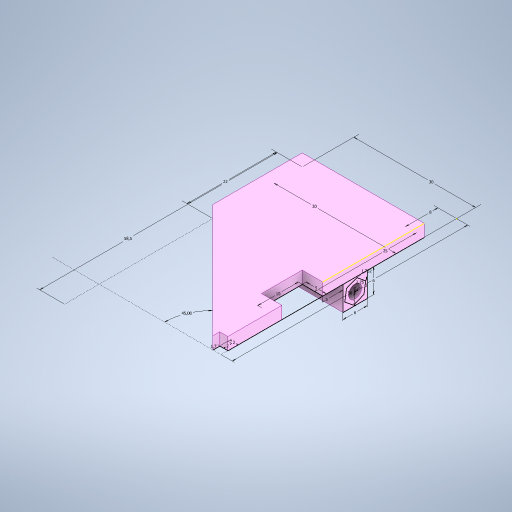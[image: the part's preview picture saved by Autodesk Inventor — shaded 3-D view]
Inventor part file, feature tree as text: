
AUTODESK INVENTOR PART (.ipt)
format: ipt  version: 2023 (Build 270158000, 158)  size: 310,272 bytes
history: native  units: in
note: dims shown in document units (in); Inventor stores cm internally (conversion verified against a paired STEP export)
features: extrude x4, sketch x2, other x1, hole x1, chamfer x1
ambient origin geometry x8: Origin, YZ Plane, XZ Plane, XY Plane, X Axis, Y Axis, Z Axis, Center Point
bodies: Body1 (feature_tree)
feature tree (9):
  other  "Bryła1"
  sketch  "Szkic1"
  extrude  "Wyciągnięcie proste1"  Depth=0.0787in
  extrude  "Wyciągnięcie proste2"  Depth=0.0787in
  sketch  "Sketch2"  dims[d0=2.2835in d1=0.0787in d2=0.0669in d4=45.0deg d5=0.1181in d6=0.0in d7=0.0787in d8=0.1969in d9=0.3937in d10=0.3937in d11=0.0in d13=1.1811in d14=0.8661in d15=2.3031in d16=1.1811in d17=0.9843in d18=0.315in d43=0.2362in d44=0.2362in d45=0.1969in d50=0.7874in d51=0.0in d54=0.126in d55=0.2362in d56=0.1575in d57=0.0787in d58=90.0deg d59=1.1811in d60=0.0in d65=0.1181in d66=0.1181in d67=0.1083in d68=0.0682in d69=0.2362in d70=0.0in d71=0.2362in d72=0.0787in d73=45.0deg]
  extrude  "Extrusion5"  TaperAngle=45.0deg  [1 undecoded]
  hole  "Hole2"  [1 undecoded]
  extrude  "Extrusion7"  Depth=0.0787in
  chamfer  "Chamfer4"  Distance=0.1969in
note: 2 required parameter values undecoded (feature->parameter linkage not recoverable at this tier; creation-order binding heuristic only, values carry confidence <= 0.55)
